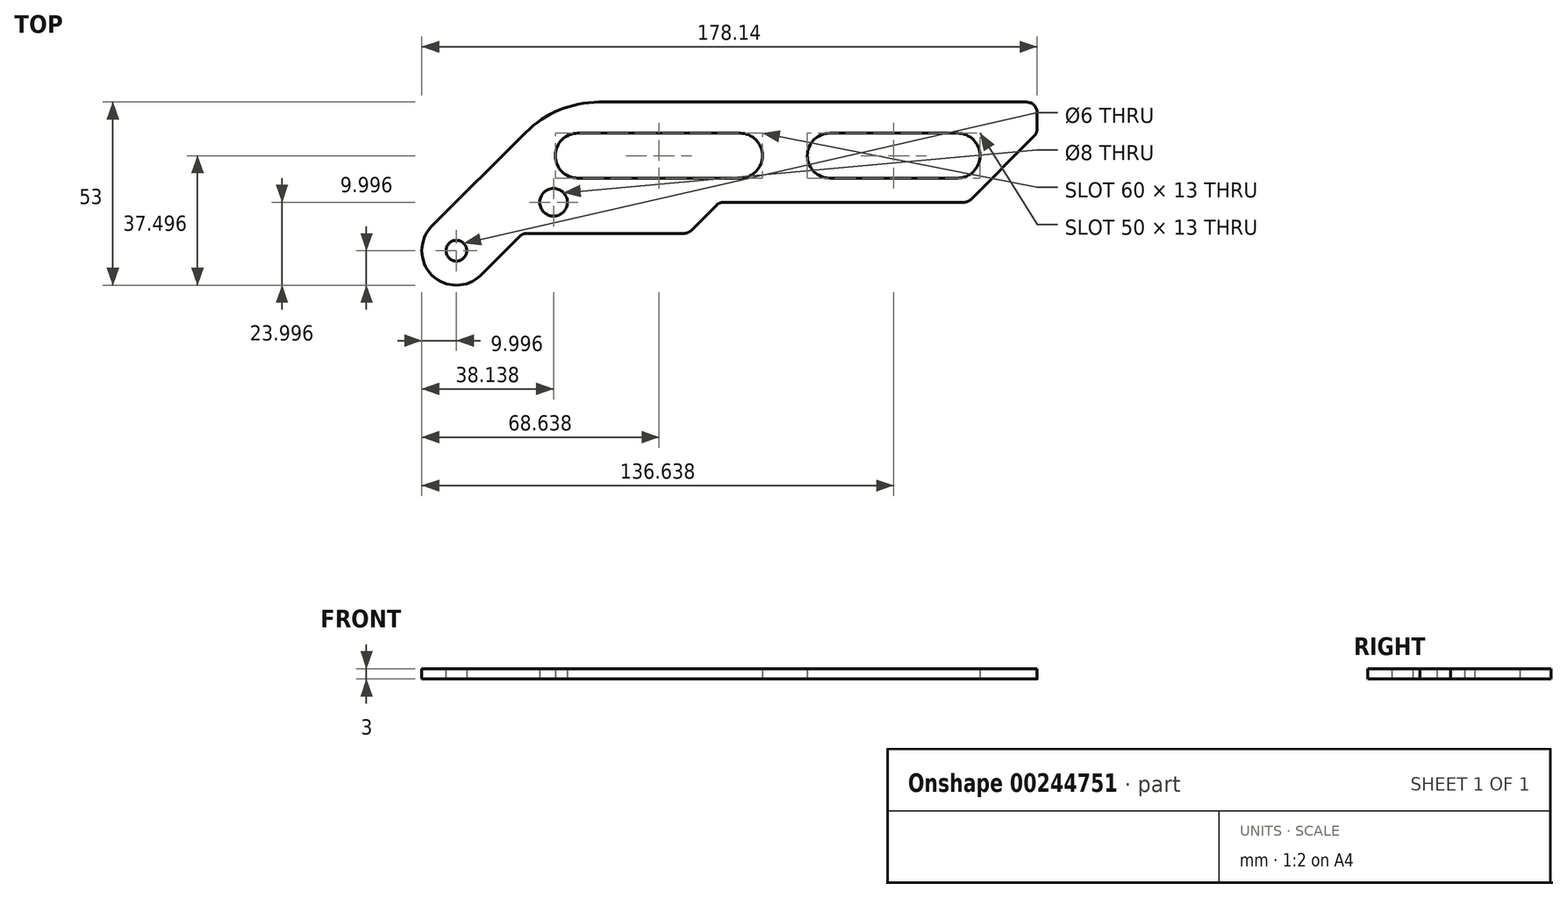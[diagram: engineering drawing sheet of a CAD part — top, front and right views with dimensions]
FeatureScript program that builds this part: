
annotation { "Feature Type Name" : "Feature", "Feature Type Description" : "" }
export const myFeature = defineFeature(function(context is Context, id is Id, definition is map)
    precondition{}
    {
        {
            var Q0;
            Q0=qCreatedBy(makeId("Top.planeOp"),FACE);
            var sketch = newSketch(context, id + "F0", { "sketchPlane" : qUnion([Q0])});
            skLineSegment(sketch, "E0", {"start": v(-352.57, 8.85) * mm, "end": v(-325.42, 35.99) * mm});
            skLineSegment(sketch, "E1", {"start": v(-304.21, 44.78) * mm, "end": v(-180.35, 44.78) * mm});
            skLineSegment(sketch, "E2", {"start": v(-177.35, 41.78) * mm, "end": v(-177.35, 37.02) * mm});
            skLineSegment(sketch, "E3", {"start": v(-178.23, 34.9) * mm, "end": v(-196.47, 16.65) * mm});
            skLineSegment(sketch, "E4", {"start": v(-198.6, 15.78) * mm, "end": v(-268.1, 15.78) * mm});
            skLineSegment(sketch, "E5", {"start": v(-270.23, 14.9) * mm, "end": v(-277.47, 7.65) * mm});
            skLineSegment(sketch, "E6", {"start": v(-279.6, 6.78) * mm, "end": v(-325.1, 6.78) * mm});
            skLineSegment(sketch, "E7", {"start": v(-327.23, 5.9) * mm, "end": v(-338.42, -5.3) * mm});
            skLineSegment(sketch, "E8", {"start": v(-310.35, 35.78) * mm, "end": v(-263.35, 35.78) * mm});
            skLineSegment(sketch, "E9", {"start": v(-263.35, 22.78) * mm, "end": v(-310.35, 22.78) * mm});
            skLineSegment(sketch, "E10", {"start": v(-237.35, 35.78) * mm, "end": v(-200.35, 35.78) * mm});
            skLineSegment(sketch, "E11", {"start": v(-237.35, 22.78) * mm, "end": v(-200.35, 22.78) * mm});
            skArc(sketch, "E12", {"start": v(-352.57, 8.85) * mm, "mid": v(-352.57, -5.3) * mm, "end": v(-338.42, -5.3) * mm});
            skArc(sketch, "E13", {"start": v(-310.35, 35.78) * mm, "mid": v(-316.85, 29.28) * mm, "end": v(-310.35, 22.78) * mm});
            skArc(sketch, "E14", {"start": v(-263.35, 22.78) * mm, "mid": v(-256.85, 29.28) * mm, "end": v(-263.35, 35.78) * mm});
            skArc(sketch, "E15", {"start": v(-237.35, 35.78) * mm, "mid": v(-243.85, 29.28) * mm, "end": v(-237.35, 22.78) * mm});
            skArc(sketch, "E16", {"start": v(-200.35, 22.78) * mm, "mid": v(-193.85, 29.28) * mm, "end": v(-200.35, 35.78) * mm});
            skCircle(sketch, "E17", {"center": v(-345.5, 1.78) * mm, "radius": 3 * mm});
            skCircle(sketch, "E18", {"center": v(-317.35, 15.78) * mm, "radius": 4 * mm});
            skArc(sketch, "E19", {"start": v(-304.21, 44.78) * mm, "mid": v(-315.7, 42.5) * mm, "end": v(-325.42, 35.99) * mm});
            skArc(sketch, "E20", {"start": v(-325.1, 6.78) * mm, "mid": v(-326.26, 6.55) * mm, "end": v(-327.23, 5.9) * mm});
            skArc(sketch, "E21", {"start": v(-279.6, 6.78) * mm, "mid": v(-278.45, 7) * mm, "end": v(-277.47, 7.65) * mm});
            skArc(sketch, "E22", {"start": v(-268.1, 15.78) * mm, "mid": v(-269.26, 15.55) * mm, "end": v(-270.23, 14.9) * mm});
            skArc(sketch, "E23", {"start": v(-198.6, 15.78) * mm, "mid": v(-197.45, 16) * mm, "end": v(-196.47, 16.65) * mm});
            skArc(sketch, "E24", {"start": v(-178.23, 34.9) * mm, "mid": v(-177.58, 35.87) * mm, "end": v(-177.35, 37.02) * mm});
            skArc(sketch, "E25", {"start": v(-177.35, 41.78) * mm, "mid": v(-178.23, 43.9) * mm, "end": v(-180.35, 44.78) * mm});
            skSolve(sketch);
        }
        {
            var Q0;
            Q0=makeQuery(id+"F0.imprint","IMPRINT",FACE,{"disambiguationData":[TD([[makeQuery(id+"F0.imprint","IMPRINT",EDGE,{"derivedFrom":sQuery(id+"F0.wireOp",EDGE,"E0")}),-1.0]])]});
            extrude(context, id + "F1", {"entities" : qUnion([Q0]), "depth" : 3 * mm});
        }
    });
